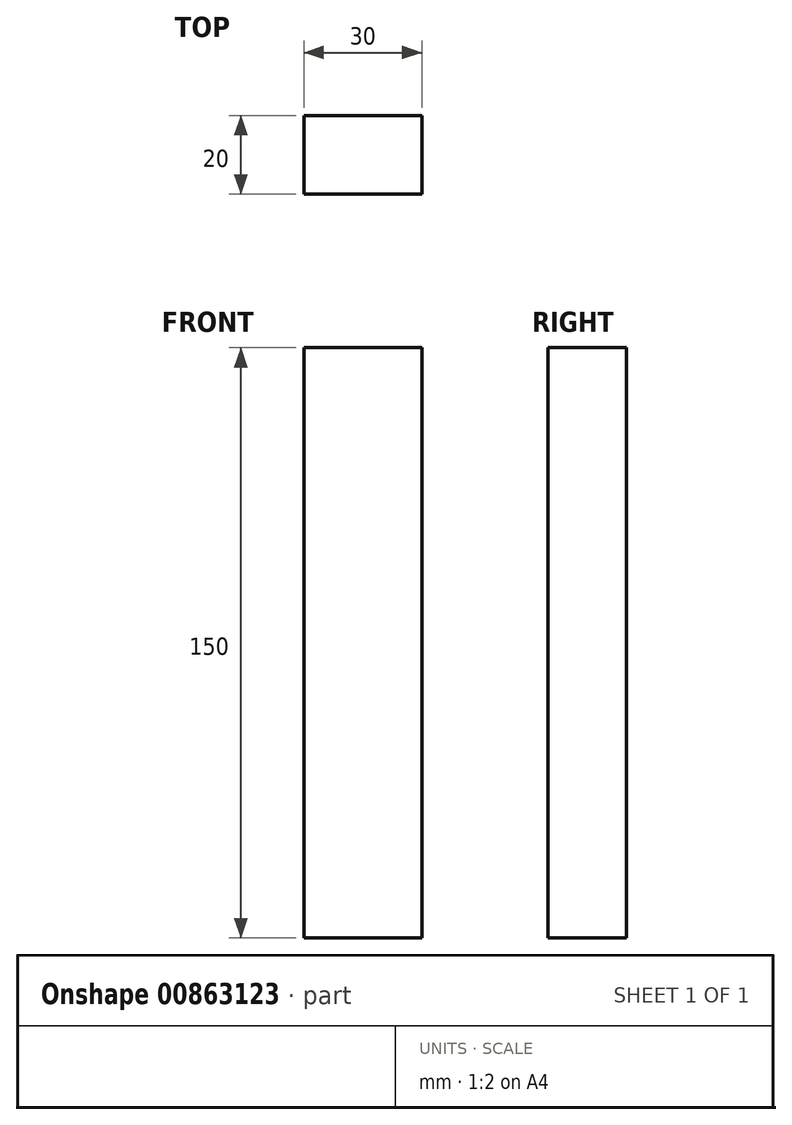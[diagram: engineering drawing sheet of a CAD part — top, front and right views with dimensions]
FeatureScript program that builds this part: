
annotation { "Feature Type Name" : "Feature", "Feature Type Description" : "" }
export const myFeature = defineFeature(function(context is Context, id is Id, definition is map)
    precondition{}
    {
        {
            var Q0;
            Q0=qCreatedBy(makeId("Top.planeOp"),FACE);
            var sketch = newSketch(context, id + "F0", { "sketchPlane" : qUnion([Q0])});
            skLineSegment(sketch, "E0", {"start": v(-17.24, 0) * mm, "end": v(12.76, 0) * mm});
            skLineSegment(sketch, "E1", {"start": v(12.76, 0) * mm, "end": v(12.76, 20) * mm});
            skLineSegment(sketch, "E2", {"start": v(12.76, 20) * mm, "end": v(-17.24, 20) * mm});
            skLineSegment(sketch, "E3", {"start": v(-17.24, 20) * mm, "end": v(-17.24, 0) * mm});
            skSolve(sketch);
        }
        {
            var Q0;
            Q0=makeQuery(id+"F0.imprint","IMPRINT",FACE,{"disambiguationData":[TD([[makeQuery(id+"F0.imprint","IMPRINT",EDGE,{"derivedFrom":sQuery(id+"F0.wireOp",EDGE,"E0")}),1.0]])]});
            extrude(context, id + "F1", {"entities" : qUnion([Q0]), "depth" : 150 * mm, "offsetDistance" : 25 * mm});
        }
    });
